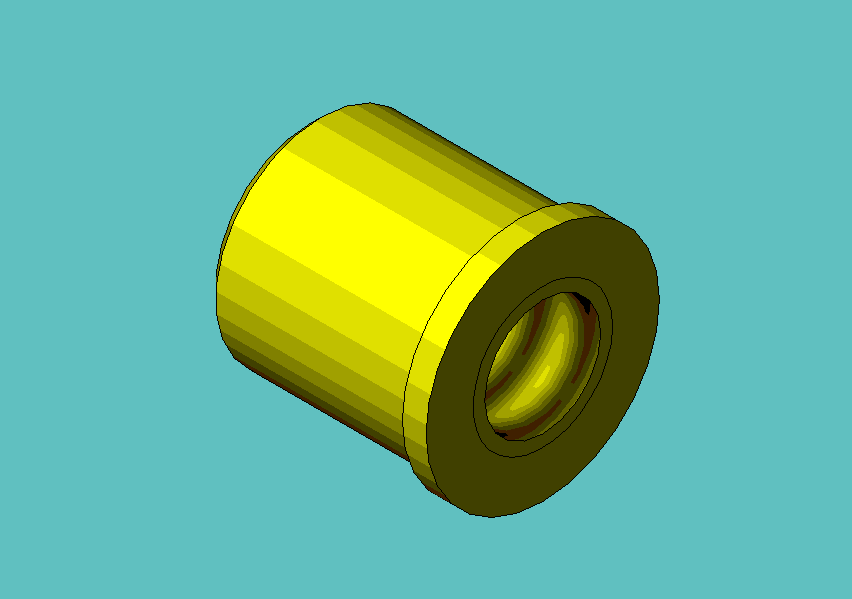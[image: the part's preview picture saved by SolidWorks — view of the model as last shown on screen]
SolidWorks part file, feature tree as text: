
SOLIDWORKS PART (.sldprt)
format: sldprt  version: not decoded by parser v0  size: 104,448 bytes
history: native  units: mm
features: sketch x3, material x1, revolve x1, hole x1, thread x1 (+12 scaffold rows collapsed)
feature tree (19):
  scaffold x12  (default folders/planes/origin — collapsed)
  material  "Material <not specified>"
  sketch  "Sketch1"  dims[D1=5.0038mm]
  revolve  "Revolve1"  Angle=360deg
  hole  "M3x0.25-4h Tapped Hole1"  Diameter=2.4892mm Depth=5.0038mm
  sketch  "3DSketch1"
  sketch  "Sketch3"  dims[hole-wizard template sketch: 59 standard entries collapsed; hole parameters kept: c18.Thru Tap Drill Dia.=2.4892mm c18.Thru Tap Drill Depth=5.0038mm]
  thread  "Hole Thread1"  Diameter=2.9972mm  [1 undecoded]
decode coverage: 5 of 6 modeling features carry decoded parameters
note: ~ marks probable driven/reference dimensions
note: 1 parameter value undecoded
note: suppression state not decoded; provenance and decode notes live in map.json
